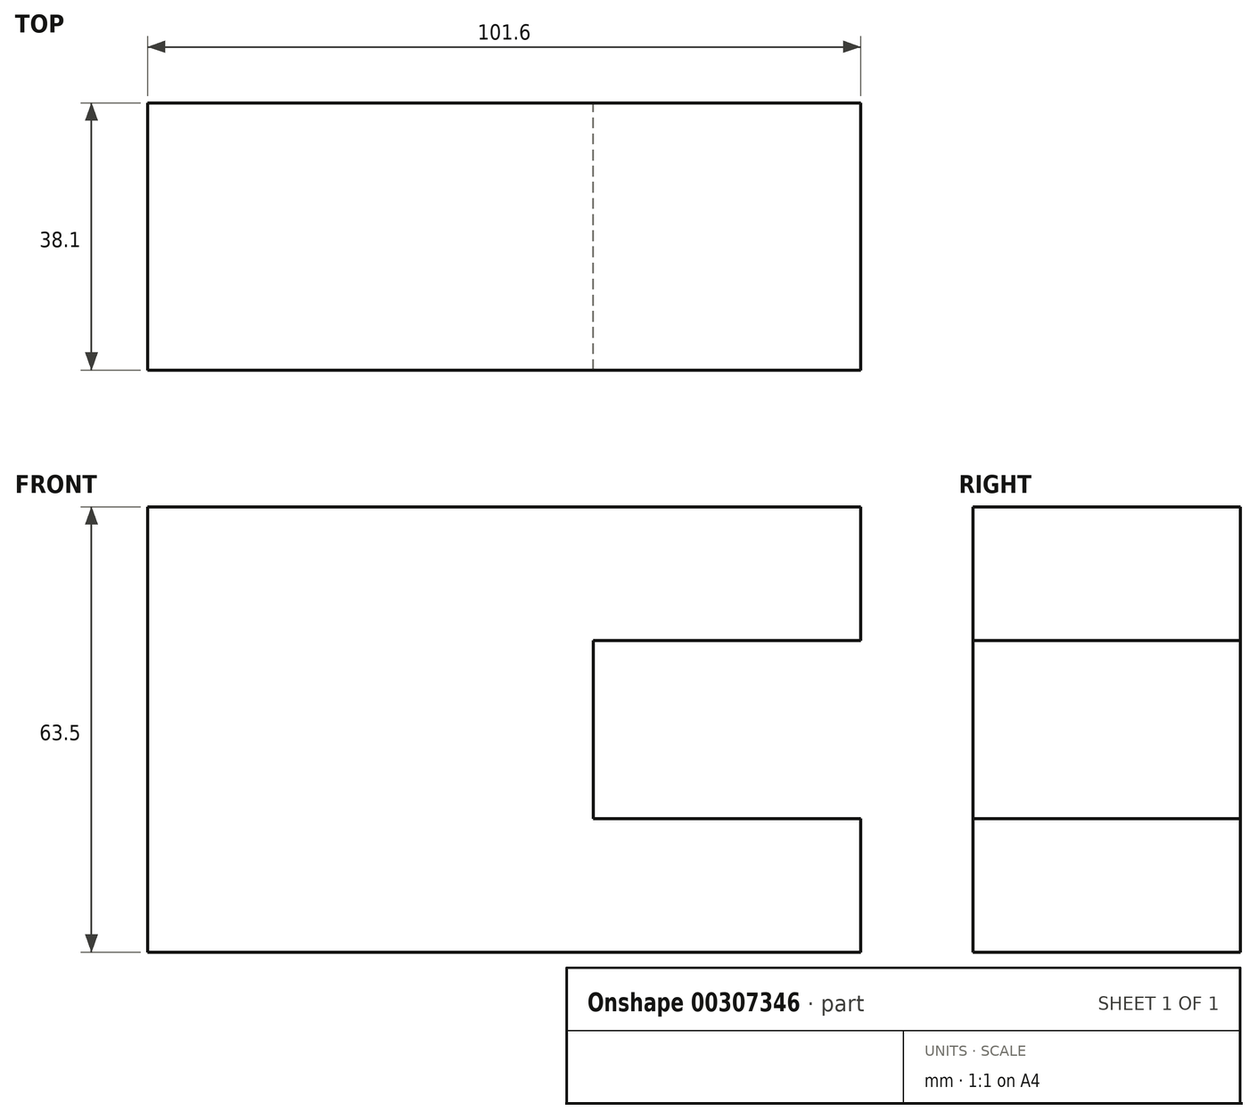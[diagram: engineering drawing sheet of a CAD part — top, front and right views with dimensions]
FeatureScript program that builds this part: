
annotation { "Feature Type Name" : "Feature", "Feature Type Description" : "" }
export const myFeature = defineFeature(function(context is Context, id is Id, definition is map)
    precondition{}
    {
        {
            var Q0;
            Q0=qCreatedBy(makeId("Front.planeOp"),FACE);
            var sketch = newSketch(context, id + "F0", { "sketchPlane" : qUnion([Q0])});
            skLineSegment(sketch, "E0", {"start": v(-49.94, -22.6) * mm, "end": v(51.66, -22.6) * mm});
            skLineSegment(sketch, "E1", {"start": v(51.66, -22.6) * mm, "end": v(51.66, -3.55) * mm});
            skLineSegment(sketch, "E2", {"start": v(51.66, -3.55) * mm, "end": v(13.56, -3.55) * mm});
            skLineSegment(sketch, "E3", {"start": v(13.56, -3.55) * mm, "end": v(13.56, 21.85) * mm});
            skLineSegment(sketch, "E4", {"start": v(13.56, 21.85) * mm, "end": v(51.66, 21.85) * mm});
            skLineSegment(sketch, "E5", {"start": v(51.66, 21.85) * mm, "end": v(51.66, 40.9) * mm});
            skLineSegment(sketch, "E6", {"start": v(51.66, 40.9) * mm, "end": v(-49.94, 40.9) * mm});
            skLineSegment(sketch, "E7", {"start": v(-49.94, 40.9) * mm, "end": v(-49.94, -22.6) * mm});
            skSolve(sketch);
        }
        {
            var Q0;
            Q0=makeQuery(id+"F0.imprint","IMPRINT",FACE,{"disambiguationData":[TD([[makeQuery(id+"F0.imprint","IMPRINT",EDGE,{"derivedFrom":sQuery(id+"F0.wireOp",EDGE,"E0")}),1.0]])]});
            extrude(context, id + "F1", {"entities" : qUnion([Q0]), "depth" : 38.1 * mm});
        }
    });
